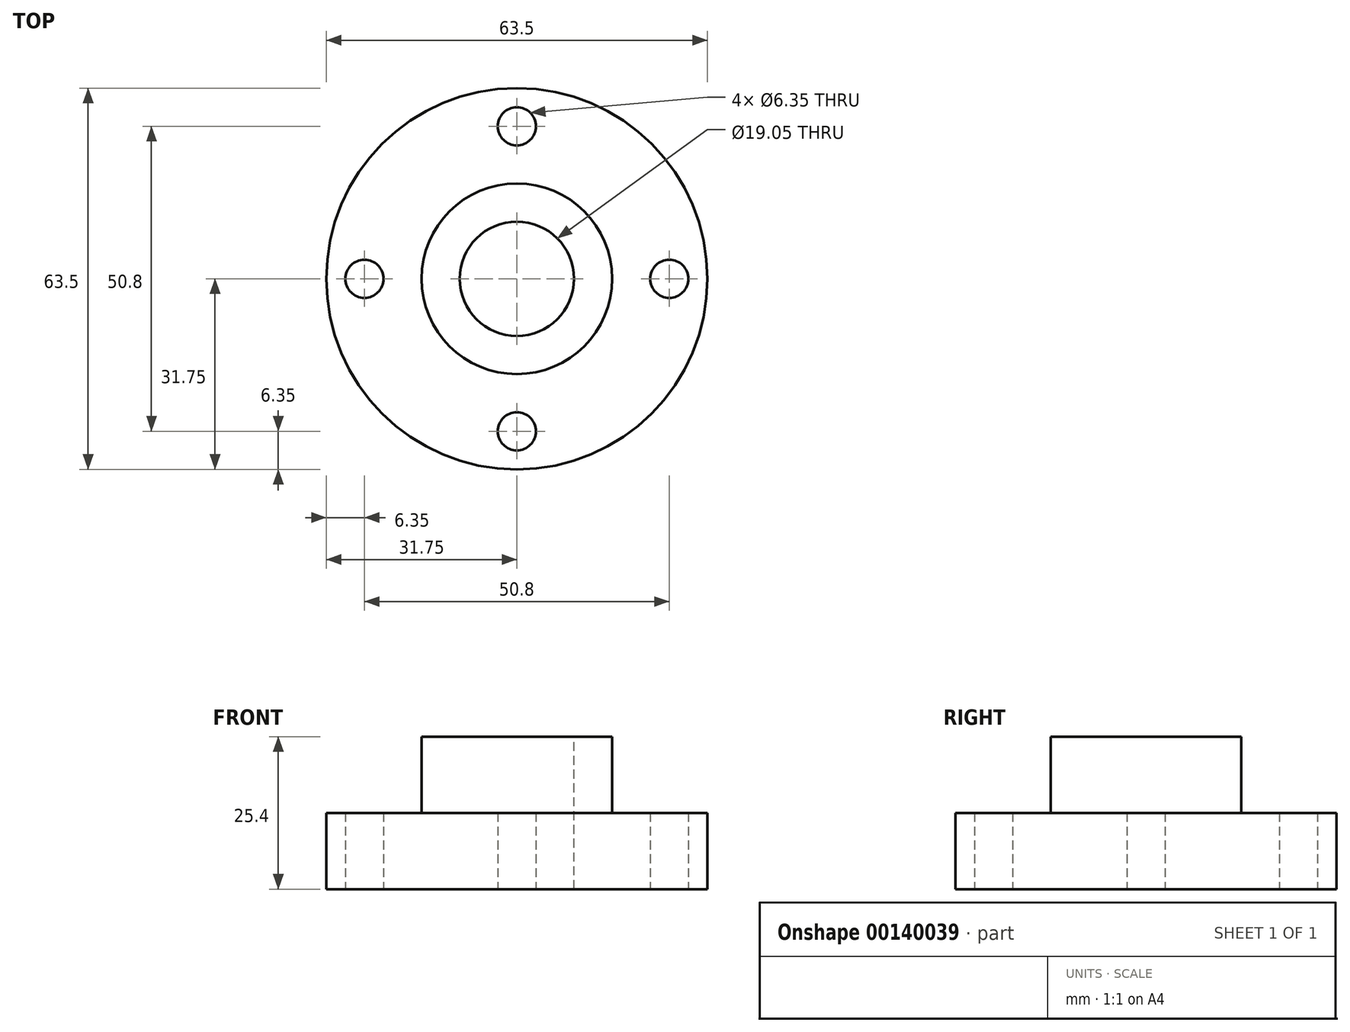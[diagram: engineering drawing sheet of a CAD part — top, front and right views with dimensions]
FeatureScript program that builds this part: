
annotation { "Feature Type Name" : "Feature", "Feature Type Description" : "" }
export const myFeature = defineFeature(function(context is Context, id is Id, definition is map)
    precondition{}
    {
        {
            var Q0;
            Q0=qCreatedBy(makeId("Top.planeOp"),FACE);
            var sketch = newSketch(context, id + "F0", { "sketchPlane" : qUnion([Q0])});
            skCircle(sketch, "E0", {"center": v(0, 0) * mm, "radius": 31.75 * mm});
            skLineSegment(sketch, "E1", {"start": v(-48.38, 0) * mm, "end": v(59.82, 0) * mm, "construction": true});
            skLineSegment(sketch, "E2", {"start": v(0, 42.9) * mm, "end": v(0, -51) * mm, "construction": true});
            skCircle(sketch, "E3", {"center": v(0, 0) * mm, "radius": 25.4 * mm, "construction": true});
            skCircle(sketch, "E4", {"center": v(0, 0) * mm, "radius": 15.88 * mm});
            skCircle(sketch, "E5", {"center": v(-25.4, 0) * mm, "radius": 3.18 * mm});
            skCircle(sketch, "E6", {"center": v(0, -25.4) * mm, "radius": 3.18 * mm});
            skCircle(sketch, "E7", {"center": v(25.4, 0) * mm, "radius": 3.18 * mm});
            skCircle(sketch, "E8", {"center": v(0, 25.4) * mm, "radius": 3.18 * mm});
            skSolve(sketch);
        }
        {
            var Q0;
            Q0=makeQuery(id+"F0.imprint","IMPRINT",FACE,{"disambiguationData":[TD([[makeQuery(id+"F0.imprint","IMPRINT",EDGE,{"derivedFrom":sQuery(id+"F0.wireOp",EDGE,"E0")}),1.0]])]});
            extrude(context, id + "F1", {"entities" : qUnion([Q0]), "depth" : 12.7 * mm});
        }
        {
            var Q0;
            Q0=makeQuery(id+"F0.imprint","IMPRINT",FACE,{"disambiguationData":[TD([[makeQuery(id+"F0.imprint","IMPRINT",EDGE,{"derivedFrom":sQuery(id+"F0.wireOp",EDGE,"E4")}),1.0]])]});
            extrude(context, id + "F2", {"entities" : qUnion([Q0]), "operationType" : NewBodyOperationType.ADD, "depth" : 25.4 * mm});
        }
        {
            var Q0;
            Q0=makeQuery(id+"F2.opExtrude","CAP_FACE",FACE,{"disambiguationData":[OSD([sQuery(id+"F0.wireOp",EDGE,"E4")])],"isStart":false});
            var sketch = newSketch(context, id + "F3", { "sketchPlane" : qUnion([Q0])});
            skCircle(sketch, "E9", {"center": v(0, 0) * mm, "radius": 9.53 * mm});
            skSolve(sketch);
        }
        {
            var Q0;
            Q0=makeQuery(id+"F3.imprint","IMPRINT",FACE,{"disambiguationData":[TD([[makeQuery(id+"F3.imprint","IMPRINT",EDGE,{"derivedFrom":sQuery(id+"F3.wireOp",EDGE,"E9")}),1.0]])]});
            extrude(context, id + "F4", {"entities" : qUnion([Q0]), "operationType" : NewBodyOperationType.REMOVE, "endBound" : BoundingType.THROUGH_ALL, "oppositeDirection" : true, "depth" : 25.4 * mm});
        }
    });
